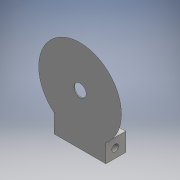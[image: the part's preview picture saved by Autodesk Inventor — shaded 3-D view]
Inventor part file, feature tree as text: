
AUTODESK INVENTOR PART (.ipt)
format: ipt  version: 2016 (Build 200138000, 138)  size: 166,912 bytes
history: native  units: mm
features: sketch x8, extrude x6, revolve x1, hole x1
ambient origin geometry x8: Origin, YZ Plane, XZ Plane, XY Plane, X Axis, Y Axis, Z Axis, Center Point
bodies: Solid1 (feature_tree)
feature tree (16):
  revolve  "Revolution1"  [1 undecoded]
  extrude  "Extrusion1"  TaperAngle=90.0deg  [1 undecoded]
  extrude  "Extrusion2"  Depth=8.0mm
  extrude  "Extrusion3"  Depth=3.0mm TaperAngle=0.0deg
  extrude  "Extrusion4"  Depth=6.0mm TaperAngle=0.0deg
  extrude  "Extrusion5"  Depth=10.0mm
  extrude  "Extrusion6"  Depth=6.0mm
  hole  "Hole1"  [1 undecoded]
  sketch  "Sketch1"  dims[d0=22.0mm d1=2.0mm]
  sketch  "Sketch2"  dims[d2=5.0mm d3=90.0deg]
  sketch  "Sketch3"  dims[d4=0.5mm d5=0.0mm d6=8.0mm]
  sketch  "Sketch4"  dims[d7=0.5mm d8=0.0mm d12=3.0mm d13=0.0mm]
  sketch  "Sketch5"  dims[d14=6.0mm d15=0.0mm d19=6.0mm d20=0.0mm]
  sketch  "Sketch6"  dims[d21=10.0mm d22=0.0mm d23=4.35mm]
  sketch  "Sketch7"  dims[d24=6.0mm d25=6.0mm]
  sketch  "Sketch9"  dims[d26=4.35mm d27=6.0mm d28=4.0mm d29=2.0mm d30=90.0deg d31=8.0mm d32=20.594885mm]
note: 3 required parameter values undecoded (feature->parameter linkage not recoverable at this tier; creation-order binding heuristic only, values carry confidence <= 0.55)